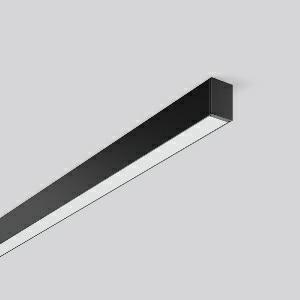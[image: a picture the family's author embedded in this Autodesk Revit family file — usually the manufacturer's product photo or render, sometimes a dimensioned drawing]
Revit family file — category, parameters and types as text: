
# Revit family: less_is_more_27_312198_003_8b3a
name_source: partatom
category: Lighting Fixtures
units: mm (PartAtom-declared; Revit-internal decimal feet)

## family parameters
Cut with Voids When Loaded = No
Host = Face
Light Source = No
Part Type = Normal
Room Calculation Point = No
Round Connector Dimension = Use Diameter
Shared = No

## types (1)
- LESS IS MORE 27 (1 x LED Modul 830, 1900 lm, 3000)
    Apparent Load = 35 VA
    CIE Flux Codes = 48 79 96 100 100
    Color Rendering = 80
    Color Temperature = 3000
    Default Elevation = 1800 mm
    Description = Series: LESS IS MORE 27
Ceiling and wall luminaire with slim design. Housing: extruded aluminium profile, powder-coated. End cap aluminium powder-coated. Diffuser made of non-yellowing plastic (PMMA), opal. Suitable for Ceiling mounting, Wall (surface). External driver with connecting cable. 
Colour: deep black, matt (RAL 9005)
Length: 1212 mm
Width: 28 mm
Height: 38 mm
Lamp: LED
Socket: without socket
Colour temperature: 3000K
Colour rendering index (CRI): 82
System power: 35 W
Rated luminous flux: 1900 lm
Luminous efficiency: 54 lm/W
Control gear: Regulated power supply
Protection class: II
Type of protection: IP 20
    Height = 38 mm
    Lamp = 1 x LED Modul 830
    Lamp Light Flux = 1900 lm
    Lamp count = 1
    Length = 1212 mm
    Lifetime = 50000 h
    Luminous efficacy = 54 lm/W
    Manufacturer = RZB
    ModVariant = No
    Model = 312198.003
    Mounting Place = Ceiling, Wall
    Mounting Type = Surface mounted
    Number of Poles = 1
    OnlyDefault = Yes
    Power Factor = 1
    Product Name = LESS IS MORE 27
    Product group = Surface mounted LED linear luminaires
    ProductGroupID = 307
    Protection Class = Protection class II
    Protection Degree = IP 20
    RLX_Detail_Level = 1
    RLX_Emergency_Light_Flux = 0 lm
    RLX_Emergency_Type = 0
    RLX_Emergency_Type_DB = No
    RlxData = <blob elided: 28633 chars, md5=7c88a202>
    Socket = socket
    Standby Power = 0 W
    System Light Flux = 1900 lm
    System Power = 35 W
    Type Comments = Product without accessories
    Type Image = 312196.003.jpg
    URL = http://relux.com
    VarID = ---
    Voltage = 230 V
    Voltage Range = 220-240 V
    Weight = 0.00 kg
    Width = 28 mm

## geometry (parser evidence)
native form markers: Blend x4, Sweep x11
no freeform markers — native parametric forms only
